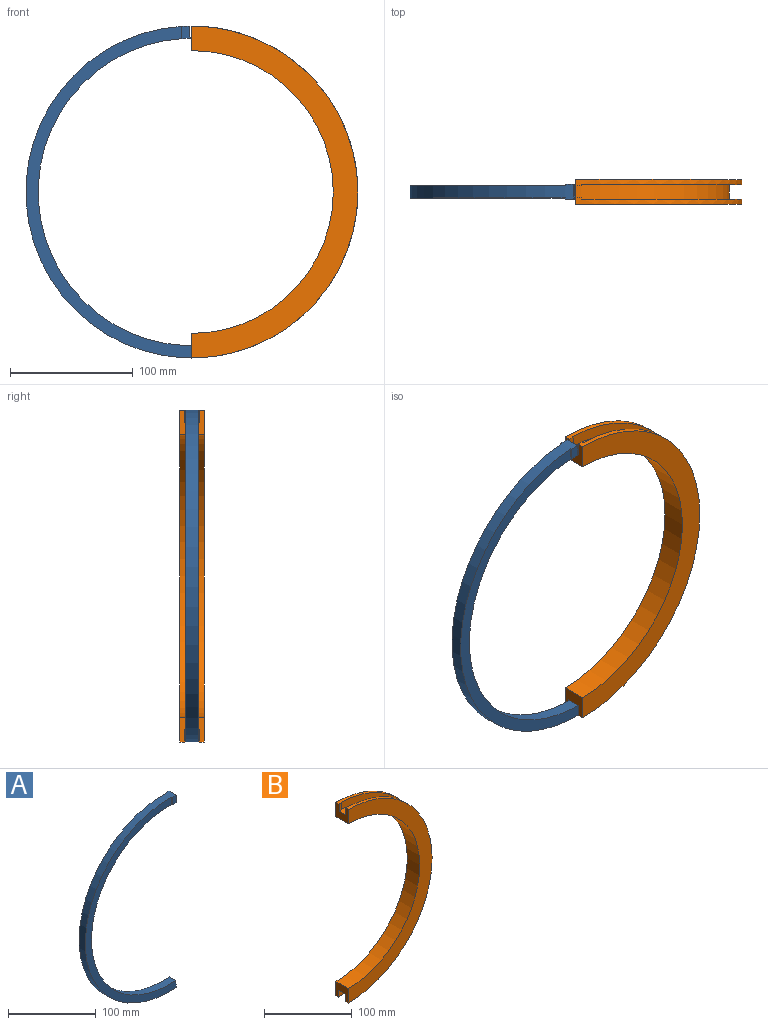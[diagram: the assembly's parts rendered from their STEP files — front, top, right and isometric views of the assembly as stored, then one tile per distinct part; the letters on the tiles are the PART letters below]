
ASSEMBLY  parts=2 mates=1
PART A: 10 faces, bbox 146.8x12x270 mm
  f0: cylinder r=135mm len=270mm, axis (0,1,0), area 4490.9mm2, adj f1,f3,f4,f5,f6,f7,f8,f9
  f1: plane 10x9.96mm, normal (1,0,0.09), area 100mm2, adj f0,f2,f4,f5
  f2: cylinder r=125mm len=250mm, axis (0,1,0), area 4158.2mm2, adj f1,f3,f4,f5,f6,f7,f8,f9
  f3: plane 12x9.96mm, normal (1,0,-0.09), area 120mm2, adj f0,f2,f6,f9
  f4: plane 270x146.77mm, normal (0,-1,0), area 4242.9mm2, adj f0,f1,f2,f8
  f5: plane 270x146.77mm, normal (0,1,0), area 4242.9mm2, adj f0,f1,f2,f7
  f6: plane 10.39x7.4mm, normal (0,1,0), area 68.1mm2, adj f0,f2,f3,f7
  f7: plane 9.99x1mm, normal (-1,0,0.03), area 10mm2, adj f0,f2,f5,f6
  f8: plane 9.99x1mm, normal (-1,0,0.03), area 10mm2, adj f0,f2,f4,f9
  f9: plane 10.39x7.4mm, normal (0,-1,0), area 68.1mm2, adj f0,f2,f3,f8
PART B: 14 faces, bbox 135x20x270 mm
  f0: cylinder r=135mm len=270mm, axis (0,1,0), area 1701.2mm2, adj f2,f4,f6,f7,f11,f12
  f1: cylinder r=115mm len=230mm, axis (0,1,0), area 7225.7mm2, adj f2,f4,f5,f6
  f2: plane 20x20mm, normal (-1,0,0), area 280mm2, adj f0,f1,f3,f5,f6,f9,f12,f13
  f3: cylinder r=135mm len=270mm, axis (0,1,0), area 1701.2mm2, adj f2,f4,f5,f8,f10,f13
  f4: plane 20x20mm, normal (-1,0,0), area 300mm2, adj f0,f1,f3,f5,f6,f7,f8,f9
  f5: plane 270x135mm, normal (0,-1,0), area 7854mm2, adj f1,f2,f3,f4
  f6: plane 270x135mm, normal (0,1,0), area 7854mm2, adj f0,f1,f2,f4
  f7: plane 10.08x4.71mm, normal (0,-1,0), area 45.4mm2, adj f0,f4,f9,f11
  f8: plane 10.08x4.71mm, normal (0,1,0), area 45.4mm2, adj f3,f4,f9,f10
  f9: cylinder r=125mm len=250mm, axis (0,-1,0), area 4703.7mm2, adj f2,f4,f7,f8,f10,f11,f12,f13
  f10: plane 9.99x1mm, normal (1,0,-0.03), area 10mm2, adj f3,f8,f9,f13
  f11: plane 9.99x1mm, normal (1,0,-0.03), area 10mm2, adj f0,f7,f9,f12
  f12: plane 269.92x135mm, normal (0,-1,0), area 4038.7mm2, adj f0,f2,f9,f11
  f13: plane 269.92x135mm, normal (0,1,0), area 4038.7mm2, adj f2,f3,f9,f10
PLACE A rot(axis=(0,-1,0),5.7deg) t=(0,0,0)mm
PLACE B at identity fixed
MATE revolute B.f9 <-> A.f2  axis (0,-1,0) through (0,0,0)mm
